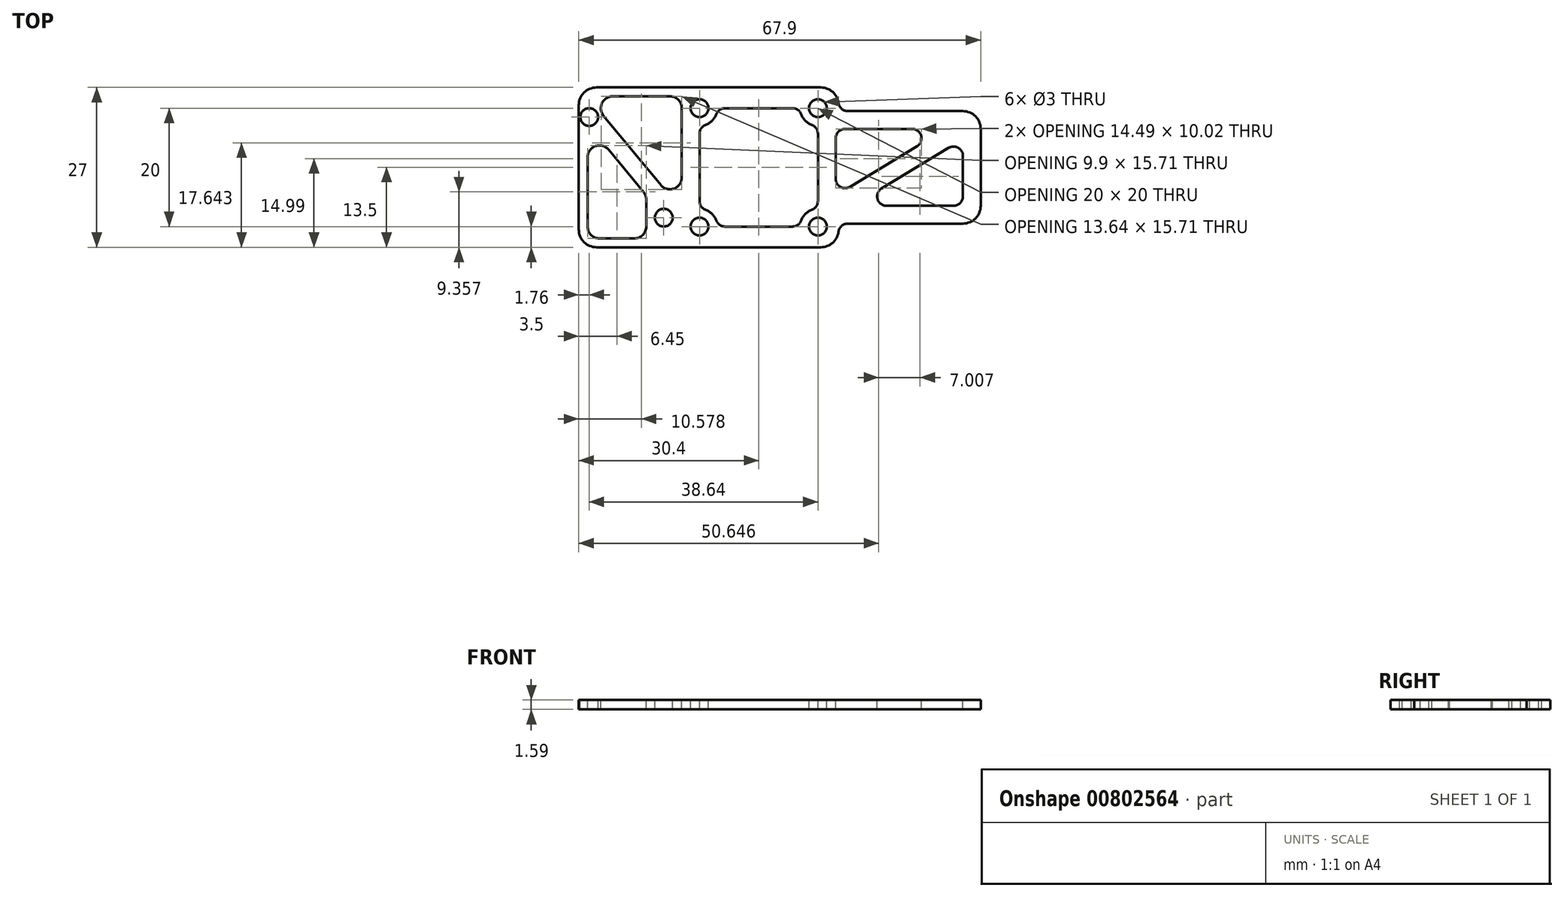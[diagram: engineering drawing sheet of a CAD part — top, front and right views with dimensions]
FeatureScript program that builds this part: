
annotation { "Feature Type Name" : "Feature", "Feature Type Description" : "" }
export const myFeature = defineFeature(function(context is Context, id is Id, definition is map)
    precondition{}
    {
        {
            var Q0;
            Q0=qCreatedBy(makeId("Top.planeOp"),FACE);
            var sketch = newSketch(context, id + "F0", { "sketchPlane" : qUnion([Q0])});
            skLineSegment(sketch, "E0.bottom", {"start": v(-13.5, 13.5) * mm, "end": v(10.5, 13.5) * mm});
            skLineSegment(sketch, "E0.top", {"start": v(-13.5, -13.5) * mm, "end": v(10.5, -13.5) * mm});
            skPoint(sketch, "E0.middle", {"position": v(0, 0) * mm});
            skLineSegment(sketch, "E1.bottom", {"start": v(-13.5, 13.5) * mm, "end": v(-27.4, 13.5) * mm});
            skLineSegment(sketch, "E1.top", {"start": v(-13.5, -13.5) * mm, "end": v(-27.4, -13.5) * mm});
            skLineSegment(sketch, "E1.right", {"start": v(-30.4, 10.5) * mm, "end": v(-30.4, -10.5) * mm});
            skPoint(sketch, "E2", {"position": v(-28.64, 8.5) * mm});
            skPoint(sketch, "E3", {"position": v(-16.04, -8.5) * mm});
            skLineSegment(sketch, "E4", {"start": v(-40.32, 0) * mm, "end": v(-13.07, 0) * mm, "construction": true});
            skLineSegment(sketch, "E5.bottom", {"start": v(-10, 10) * mm, "end": v(10, 10) * mm, "construction": true});
            skLineSegment(sketch, "E5.top", {"start": v(-10, -10) * mm, "end": v(10, -10) * mm, "construction": true});
            skLineSegment(sketch, "E5.left", {"start": v(-10, 10) * mm, "end": v(-10, -10) * mm, "construction": true});
            skLineSegment(sketch, "E5.right", {"start": v(10, 10) * mm, "end": v(10, -10) * mm, "construction": true});
            skPoint(sketch, "E6.visualSharp", {"position": v(-30.4, 13.5) * mm});
            skArc(sketch, "E6.filletArc", {"start": v(-27.4, 13.5) * mm, "mid": v(-29.52, 12.62) * mm, "end": v(-30.4, 10.5) * mm});
            skPoint(sketch, "E7.visualSharp", {"position": v(13.5, 13.5) * mm});
            skArc(sketch, "E7.filletArc", {"start": v(13.48, 10.88) * mm, "mid": v(12.48, 12.75) * mm, "end": v(10.5, 13.5) * mm});
            skPoint(sketch, "E8.visualSharp", {"position": v(13.5, -13.5) * mm});
            skArc(sketch, "E8.filletArc", {"start": v(10.5, -13.5) * mm, "mid": v(12.48, -12.75) * mm, "end": v(13.48, -10.88) * mm});
            skPoint(sketch, "E9.visualSharp", {"position": v(-30.4, -13.5) * mm});
            skArc(sketch, "E9.filletArc", {"start": v(-30.4, -10.5) * mm, "mid": v(-29.52, -12.62) * mm, "end": v(-27.4, -13.5) * mm});
            skLineSegment(sketch, "E10.bottom", {"start": v(15.05, 9.5) * mm, "end": v(34.5, 9.5) * mm});
            skLineSegment(sketch, "E10.top", {"start": v(15.05, -9.5) * mm, "end": v(34.5, -9.5) * mm});
            skLineSegment(sketch, "E10.right", {"start": v(37.5, 6.5) * mm, "end": v(37.5, -6.5) * mm});
            skPoint(sketch, "E10.middle", {"position": v(25.5, 0) * mm});
            skArc(sketch, "E11", {"start": v(13.48, 10.88) * mm, "mid": v(14, 9.9) * mm, "end": v(15.05, 9.5) * mm});
            skArc(sketch, "E12", {"start": v(15.05, -9.5) * mm, "mid": v(14, -9.9) * mm, "end": v(13.48, -10.88) * mm});
            skPoint(sketch, "E10.left.start.orphan", {"position": v(13.5, 9.5) * mm});
            skPoint(sketch, "E0.right.start.orphan", {"position": v(13.5, -9.5) * mm});
            skPoint(sketch, "E13.visualSharp", {"position": v(37.5, 9.5) * mm});
            skArc(sketch, "E13.filletArc", {"start": v(37.5, 6.5) * mm, "mid": v(36.62, 8.62) * mm, "end": v(34.5, 9.5) * mm});
            skPoint(sketch, "E14.visualSharp", {"position": v(37.5, -9.5) * mm});
            skArc(sketch, "E14.filletArc", {"start": v(34.5, -9.5) * mm, "mid": v(36.62, -8.62) * mm, "end": v(37.5, -6.5) * mm});
            skLineSegment(sketch, "E15", {"start": v(13.5, 9.5) * mm, "end": v(13.5, -9.5) * mm, "construction": true});
            skLineSegment(sketch, "E16", {"start": v(13.5, 9.5) * mm, "end": v(15.05, 9.5) * mm, "construction": true});
            skLineSegment(sketch, "E17", {"start": v(13.5, -9.5) * mm, "end": v(15.05, -9.5) * mm, "construction": true});
            skLineSegment(sketch, "E18", {"start": v(10.5, 13.5) * mm, "end": v(13.5, 13.5) * mm, "construction": true});
            skLineSegment(sketch, "E19", {"start": v(13.5, 13.5) * mm, "end": v(13.5, 9.5) * mm, "construction": true});
            skLineSegment(sketch, "E20", {"start": v(10.5, -13.5) * mm, "end": v(13.5, -13.5) * mm, "construction": true});
            skLineSegment(sketch, "E21", {"start": v(13.5, -13.5) * mm, "end": v(13.5, -9.5) * mm, "construction": true});
            skSolve(sketch);
        }
        {
            var Q0;
            Q0=makeQuery(id+"F0.imprint","IMPRINT",FACE,{"disambiguationData":[TD([[makeQuery(id+"F0.imprint","IMPRINT",EDGE,{"derivedFrom":sQuery(id+"F0.wireOp",EDGE,"E0.bottom")}),-1.0]])]});
            extrude(context, id + "F1", {"entities" : qUnion([Q0]), "oppositeDirection" : true, "depth" : 1.59 * mm, "offsetDistance" : 25 * mm});
        }
        {
            var Q0;
            Q0=sQuery(id+"F0.wireOp",VERTEX,"E5.bottom.start");
            var Q1;
            Q1=sQuery(id+"F0.wireOp",VERTEX,"E5.bottom.end");
            var Q2;
            Q2=sQuery(id+"F0.wireOp",VERTEX,"E5.right.end");
            var Q3;
            Q3=sQuery(id+"F0.wireOp",VERTEX,"E5.top.start");
            var Q4;
            Q4=makeQuery(id+"F1.opExtrude","SWEPT_BODY",BODY,{"disambiguationData":[OSD([sQuery(id+"F0.wireOp",EDGE,"E0.bottom"),sQuery(id+"F0.wireOp",EDGE,"E0.top"),sQuery(id+"F0.wireOp",EDGE,"E0.right"),sQuery(id+"F0.wireOp",EDGE,"E1.bottom"),sQuery(id+"F0.wireOp",EDGE,"E1.top"),sQuery(id+"F0.wireOp",EDGE,"E1.right"),sQuery(id+"F0.wireOp",EDGE,"E6.filletArc"),sQuery(id+"F0.wireOp",EDGE,"E7.filletArc"),sQuery(id+"F0.wireOp",EDGE,"E8.filletArc"),sQuery(id+"F0.wireOp",EDGE,"E9.filletArc")])]});
            hole(context, id + "F2", {"style" : HoleStyle.SIMPLE, "endStyle" : HoleEndStyle.BLIND, "holeDiameter" : 3 * mm, "majorDiameter" : 5 * mm, "holeDepth" : 5 * mm, "isTappedThrough" : true, "tappedDepth" : 12 * mm, "tapClearance" : 3, "locations" : qUnion([Q0, Q1, Q2, Q3]), "scope" : qUnion([Q4])});
        }
        {
            var Q0;
            Q0=sQuery(id+"F0.wireOp",VERTEX,"E2");
            var Q1;
            Q1=sQuery(id+"F0.wireOp",VERTEX,"E3");
            var Q2;
            Q2=makeQuery(id+"F1.opExtrude","SWEPT_BODY",BODY,{"disambiguationData":[OSD([sQuery(id+"F0.wireOp",EDGE,"E0.bottom"),sQuery(id+"F0.wireOp",EDGE,"E0.top"),sQuery(id+"F0.wireOp",EDGE,"E0.right"),sQuery(id+"F0.wireOp",EDGE,"E1.bottom"),sQuery(id+"F0.wireOp",EDGE,"E1.top"),sQuery(id+"F0.wireOp",EDGE,"E1.right"),sQuery(id+"F0.wireOp",EDGE,"E6.filletArc"),sQuery(id+"F0.wireOp",EDGE,"E7.filletArc"),sQuery(id+"F0.wireOp",EDGE,"E8.filletArc"),sQuery(id+"F0.wireOp",EDGE,"E9.filletArc")])]});
            hole(context, id + "F3", {"style" : HoleStyle.SIMPLE, "endStyle" : HoleEndStyle.BLIND, "holeDiameter" : 3 * mm, "majorDiameter" : 5 * mm, "holeDepth" : 5 * mm, "isTappedThrough" : true, "tappedDepth" : 12 * mm, "tapClearance" : 3, "locations" : qUnion([Q0, Q1]), "scope" : qUnion([Q2])});
        }
        {
            var Q0;
            Q0=makeQuery(id+"F0.imprint","IMPRINT",FACE,{"disambiguationData":[TD([[makeQuery(id+"F0.imprint","IMPRINT",EDGE,{"derivedFrom":sQuery(id+"F0.wireOp",EDGE,"E0.bottom")}),-1.0]])]});
            var sketch = newSketch(context, id + "F4", { "sketchPlane" : qUnion([Q0])});
            skLineSegment(sketch, "E22.bottom", {"start": v(-5.7, 10) * mm, "end": v(5.7, 10) * mm});
            skLineSegment(sketch, "E22.top", {"start": v(-5.7, -10) * mm, "end": v(5.7, -10) * mm});
            skLineSegment(sketch, "E22.left", {"start": v(-10, 5.7) * mm, "end": v(-10, -5.7) * mm});
            skLineSegment(sketch, "E22.right", {"start": v(10, 5.7) * mm, "end": v(10, -5.7) * mm});
            skArc(sketch, "E23", {"start": v(-8.96, 7.19) * mm, "mid": v(-7.88, 7.88) * mm, "end": v(-7.19, 8.96) * mm});
            skArc(sketch, "E24", {"start": v(7.19, 8.96) * mm, "mid": v(7.88, 7.88) * mm, "end": v(8.96, 7.19) * mm});
            skArc(sketch, "E25", {"start": v(8.96, -7.19) * mm, "mid": v(7.88, -7.88) * mm, "end": v(7.19, -8.96) * mm});
            skArc(sketch, "E26", {"start": v(-7.19, -8.96) * mm, "mid": v(-7.88, -7.88) * mm, "end": v(-8.96, -7.19) * mm});
            skPoint(sketch, "E27.visualSharp", {"position": v(-10, 7) * mm});
            skArc(sketch, "E27.filletArc", {"start": v(-8.96, 7.19) * mm, "mid": v(-9.71, 6.6) * mm, "end": v(-10, 5.7) * mm});
            skPoint(sketch, "E28.visualSharp", {"position": v(-7, 10) * mm});
            skArc(sketch, "E28.filletArc", {"start": v(-5.7, 10) * mm, "mid": v(-6.6, 9.71) * mm, "end": v(-7.19, 8.96) * mm});
            skPoint(sketch, "E29.visualSharp", {"position": v(7, 10) * mm});
            skArc(sketch, "E29.filletArc", {"start": v(7.19, 8.96) * mm, "mid": v(6.6, 9.71) * mm, "end": v(5.7, 10) * mm});
            skPoint(sketch, "E30.visualSharp", {"position": v(10, 7) * mm});
            skArc(sketch, "E30.filletArc", {"start": v(10, 5.7) * mm, "mid": v(9.71, 6.6) * mm, "end": v(8.96, 7.19) * mm});
            skPoint(sketch, "E31.visualSharp", {"position": v(10, -7) * mm});
            skArc(sketch, "E31.filletArc", {"start": v(8.96, -7.19) * mm, "mid": v(9.71, -6.6) * mm, "end": v(10, -5.7) * mm});
            skPoint(sketch, "E32.visualSharp", {"position": v(7, -10) * mm});
            skArc(sketch, "E32.filletArc", {"start": v(5.7, -10) * mm, "mid": v(6.6, -9.71) * mm, "end": v(7.19, -8.96) * mm});
            skPoint(sketch, "E33.visualSharp", {"position": v(-7, -10) * mm});
            skArc(sketch, "E33.filletArc", {"start": v(-7.19, -8.96) * mm, "mid": v(-6.6, -9.71) * mm, "end": v(-5.7, -10) * mm});
            skPoint(sketch, "E34.visualSharp", {"position": v(-10, -7) * mm});
            skArc(sketch, "E34.filletArc", {"start": v(-10, -5.7) * mm, "mid": v(-9.71, -6.6) * mm, "end": v(-8.96, -7.19) * mm});
            skSolve(sketch);
        }
        {
            var Q0;
            Q0=makeQuery(id+"F4.imprint","IMPRINT",FACE,{"disambiguationData":[TD([[makeQuery(id+"F4.imprint","IMPRINT",EDGE,{"derivedFrom":sQuery(id+"F4.wireOp",EDGE,"E22.bottom")}),-1.0]])]});
            extrude(context, id + "F5", {"entities" : qUnion([Q0]), "operationType" : NewBodyOperationType.REMOVE, "oppositeDirection" : true, "depth" : 25 * mm, "offsetDistance" : 25 * mm});
        }
        {
            var Q0;
            Q0=makeQuery(id+"F0.imprint","IMPRINT",FACE,{"disambiguationData":[TD([[makeQuery(id+"F0.imprint","IMPRINT",EDGE,{"derivedFrom":sQuery(id+"F0.wireOp",EDGE,"E0.bottom")}),-1.0]])]});
            var sketch = newSketch(context, id + "F6", { "sketchPlane" : qUnion([Q0])});
            skLineSegment(sketch, "E35", {"start": v(-24.66, 12) * mm, "end": v(-15, 12) * mm});
            skLineSegment(sketch, "E36", {"start": v(-13, 10) * mm, "end": v(-13, -1.71) * mm});
            skLineSegment(sketch, "E37", {"start": v(-16.54, -2.99) * mm, "end": v(-26.2, 8.73) * mm});
            skLineSegment(sketch, "E38", {"start": v(-25.36, 2.99) * mm, "end": v(-19.46, -4.17) * mm});
            skLineSegment(sketch, "E39", {"start": v(-21, -12) * mm, "end": v(-26.9, -12) * mm});
            skLineSegment(sketch, "E40", {"start": v(-28.9, -10) * mm, "end": v(-28.9, 1.71) * mm});
            skLineSegment(sketch, "E41", {"start": v(-19, -5.44) * mm, "end": v(-19, -10) * mm});
            skPoint(sketch, "E42.orphan", {"position": v(-13, -12) * mm});
            skPoint(sketch, "E43.visualSharp", {"position": v(-28.9, 7.28) * mm});
            skArc(sketch, "E43.filletArc", {"start": v(-25.36, 2.99) * mm, "mid": v(-27.58, 3.6) * mm, "end": v(-28.9, 1.71) * mm});
            skPoint(sketch, "E44.visualSharp", {"position": v(-28.9, -12) * mm});
            skArc(sketch, "E44.filletArc", {"start": v(-28.9, -10) * mm, "mid": v(-28.31, -11.41) * mm, "end": v(-26.9, -12) * mm});
            skPoint(sketch, "E45.visualSharp", {"position": v(-19, -12) * mm});
            skArc(sketch, "E45.filletArc", {"start": v(-21, -12) * mm, "mid": v(-19.59, -11.41) * mm, "end": v(-19, -10) * mm});
            skPoint(sketch, "E46.visualSharp", {"position": v(-19, -4.72) * mm});
            skArc(sketch, "E46.filletArc", {"start": v(-19, -5.44) * mm, "mid": v(-19.12, -4.77) * mm, "end": v(-19.46, -4.17) * mm});
            skPoint(sketch, "E47.visualSharp", {"position": v(-13, -7.28) * mm});
            skArc(sketch, "E47.filletArc", {"start": v(-16.54, -2.99) * mm, "mid": v(-14.32, -3.6) * mm, "end": v(-13, -1.71) * mm});
            skPoint(sketch, "E48.visualSharp", {"position": v(-13, 12) * mm});
            skArc(sketch, "E48.filletArc", {"start": v(-13, 10) * mm, "mid": v(-13.59, 11.41) * mm, "end": v(-15, 12) * mm});
            skPoint(sketch, "E49.visualSharp", {"position": v(-28.9, 12) * mm});
            skArc(sketch, "E49.filletArc", {"start": v(-24.66, 12) * mm, "mid": v(-26.47, 10.85) * mm, "end": v(-26.2, 8.73) * mm});
            skSolve(sketch);
        }
        {
            var Q0;
            Q0=makeQuery(id+"F6.imprint","IMPRINT",FACE,{"disambiguationData":[TD([[makeQuery(id+"F6.imprint","IMPRINT",EDGE,{"derivedFrom":sQuery(id+"F6.wireOp",EDGE,"E35")}),-1.0]])]});
            var Q1;
            Q1=makeQuery(id+"F6.imprint","IMPRINT",FACE,{"disambiguationData":[TD([[makeQuery(id+"F6.imprint","IMPRINT",EDGE,{"derivedFrom":sQuery(id+"F6.wireOp",EDGE,"E38")}),-1.0]])]});
            extrude(context, id + "F7", {"entities" : qUnion([Q0, Q1]), "operationType" : NewBodyOperationType.REMOVE, "oppositeDirection" : true, "depth" : 25 * mm, "offsetDistance" : 25 * mm});
        }
        {
            var Q0;
            Q0=makeQuery(id+"F0.imprint","IMPRINT",FACE,{"disambiguationData":[TD([[makeQuery(id+"F0.imprint","IMPRINT",EDGE,{"derivedFrom":sQuery(id+"F0.wireOp",EDGE,"E0.bottom")}),-1.0]])]});
            var sketch = newSketch(context, id + "F8", { "sketchPlane" : qUnion([Q0])});
            skPoint(sketch, "E50.visualSharp", {"position": v(36.5, 6.5) * mm});
            skLineSegment(sketch, "E51.bottom", {"start": v(25.9, 6.5) * mm, "end": v(14.59, 6.5) * mm});
            skLineSegment(sketch, "E51.top", {"start": v(32.91, -6.5) * mm, "end": v(21.6, -6.5) * mm});
            skLineSegment(sketch, "E51.left", {"start": v(34.5, 1.93) * mm, "end": v(34.5, -4.91) * mm});
            skLineSegment(sketch, "E51.right", {"start": v(13, 4.91) * mm, "end": v(13, -1.93) * mm});
            skPoint(sketch, "E51.middle", {"position": v(23.75, 0) * mm});
            skLineSegment(sketch, "E52", {"start": v(13, -6.5) * mm, "end": v(34.5, 6.5) * mm, "construction": true});
            skLineSegment(sketch, "E53", {"start": v(15.4, -3.3) * mm, "end": v(26.73, 3.55) * mm});
            skLineSegment(sketch, "E54", {"start": v(20.77, -3.55) * mm, "end": v(32.1, 3.3) * mm});
            skArc(sketch, "E55.filletArc", {"start": v(13, -1.93) * mm, "mid": v(13.8, -3.31) * mm, "end": v(15.4, -3.3) * mm});
            skPoint(sketch, "E56.visualSharp", {"position": v(13, 6.5) * mm});
            skArc(sketch, "E56.filletArc", {"start": v(14.59, 6.5) * mm, "mid": v(13.46, 6.04) * mm, "end": v(13, 4.91) * mm});
            skPoint(sketch, "E57.newPointA", {"position": v(34.5, 6.5) * mm});
            skArc(sketch, "E57.filletArc", {"start": v(26.73, 3.55) * mm, "mid": v(27.44, 5.34) * mm, "end": v(25.9, 6.5) * mm});
            skArc(sketch, "E58.filletArc", {"start": v(34.5, 1.93) * mm, "mid": v(33.7, 3.31) * mm, "end": v(32.1, 3.3) * mm});
            skPoint(sketch, "E59.newPointA", {"position": v(13, -6.5) * mm});
            skArc(sketch, "E59.filletArc", {"start": v(20.77, -3.55) * mm, "mid": v(20.06, -5.34) * mm, "end": v(21.6, -6.5) * mm});
            skPoint(sketch, "E60.visualSharp", {"position": v(34.5, -6.5) * mm});
            skArc(sketch, "E60.filletArc", {"start": v(32.91, -6.5) * mm, "mid": v(34.04, -6.04) * mm, "end": v(34.5, -4.91) * mm});
            skSolve(sketch);
        }
        {
            var Q0;
            Q0 = qSketchRegion(id + "F8", true);
            extrude(context, id + "F9", {"entities" : qUnion([Q0]), "operationType" : NewBodyOperationType.REMOVE, "oppositeDirection" : true, "depth" : 25 * mm, "offsetDistance" : 25 * mm});
        }
    });
